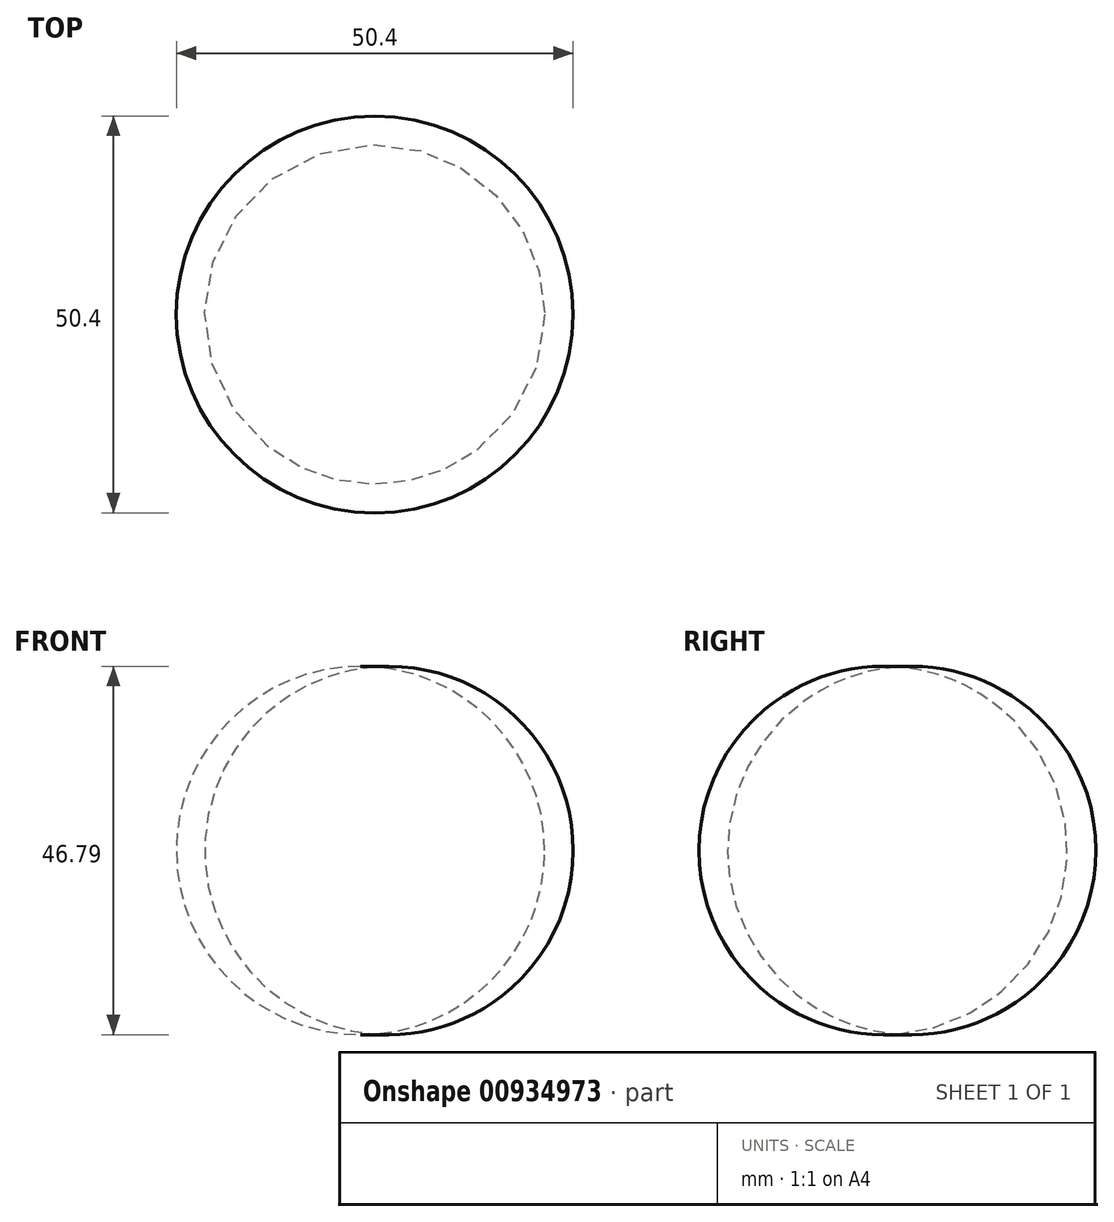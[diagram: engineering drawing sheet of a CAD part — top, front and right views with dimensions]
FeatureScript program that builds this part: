
annotation { "Feature Type Name" : "Feature", "Feature Type Description" : "" }
export const myFeature = defineFeature(function(context is Context, id is Id, definition is map)
    precondition{}
    {
        {
            var Q0;
            Q0=qCreatedBy(makeId("Front.planeOp"),FACE);
            var sketch = newSketch(context, id + "F0", { "sketchPlane" : qUnion([Q0])});
            skLineSegment(sketch, "E0", {"start": v(0, 0) * mm, "end": v(0, 46.65) * mm});
            skArc(sketch, "E1", {"start": v(0, 0) * mm, "mid": v(25.2, 23.32) * mm, "end": v(0, 46.65) * mm});
            skSolve(sketch);
        }
        {
            var Q0;
            Q0=makeQuery(id+"F0.imprint","IMPRINT",FACE,{"disambiguationData":[TD([[makeQuery(id+"F0.imprint","IMPRINT",EDGE,{"derivedFrom":sQuery(id+"F0.wireOp",EDGE,"E0")}),-1.0]])]});
            var Q1;
            Q1=sQuery(id+"F0.wireOp",EDGE,"E0");
            revolve(context, id + "F1", {"surfaceOperationType" : NewSurfaceOperationType.NEW, "entities" : qUnion([Q0]), "axis" : qUnion([Q1]), "revolveType" : RevolveType.FULL});
        }
    });
